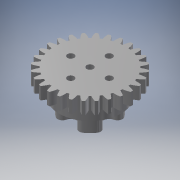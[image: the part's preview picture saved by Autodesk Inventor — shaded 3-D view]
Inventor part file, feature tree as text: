
AUTODESK INVENTOR PART (.ipt)
format: ipt  version: 2018 (Build 220112000, 112)  size: 327,680 bytes
history: native  units: mm (DEFAULTED — no unit token found)
features: sketch x7, extrude x6, plane x3, other x3, pattern_circular x1, fillet x1
ambient origin geometry x8: Origin, YZ Plane, XZ Plane, XY Plane, X Axis, Y Axis, Z Axis, Center Point
bodies: Solid1 (feature_tree)
feature tree (21):
  extrude  "Extrusion1"  Depth=5.0mm TaperAngle=0.0deg
  plane  "Work Plane2"
  plane  "Work Plane8"
  plane  "Work Plane9"
  other  "Engrenage cylindrique"
  extrude  "Extrusion4"  Depth=10.0mm TaperAngle=0.0deg
  extrude  "Extrusion5"  Depth=2.0mm
  extrude  "Extrusion2"  Depth=2.0mm TaperAngle=0.0deg
  extrude  "Extrusion3"  TaperAngle=0.0deg  [1 undecoded]
  extrude  "Extrusion6"  TaperAngle=0.0deg  [1 undecoded]
  pattern_circular  "Réseau circulaire1"  [2 undecoded]
  fillet  "Congé1"  Radius=32.0mm
  sketch  "Sketch1"  dims[d0=33.749074mm d1=5.0mm d2=0.0mm]
  sketch  "Sketch2"  dims[d3=31.438596mm d4=10.0mm d5=0.0mm d16=32.0mm d17=0.0mm d34=1.121997mm d39=0.0mm d41=0.0mm d43=32.0mm d46=32.0mm d47=0.0mm d48=0.0mm d49=2.7mm d51=0.0mm d52=17.0mm d53=2.7mm d54=7.75mm d55=10.0mm d56=0.0mm d57=40.0mm d58=360.0deg d60=20.0mm d61=25.0mm d62=5.0mm d63=0.0mm d64=20.0mm d65=11.0mm d66=0.0mm d67=12.0mm d68=0.0mm d69=5.0mm d70=11.0mm d71=0.0mm d72=2.0mm]
  other  "Srf1"
  sketch  "Esquisse4"
  sketch  "Esquisse5"
  sketch  "Esquisse6"
  sketch  "Esquisse7"
  other  "Diamètre primitif"
  sketch  "Esquisse3"
note: 4 required parameter values undecoded (feature->parameter linkage not recoverable at this tier; creation-order binding heuristic only, values carry confidence <= 0.55)
